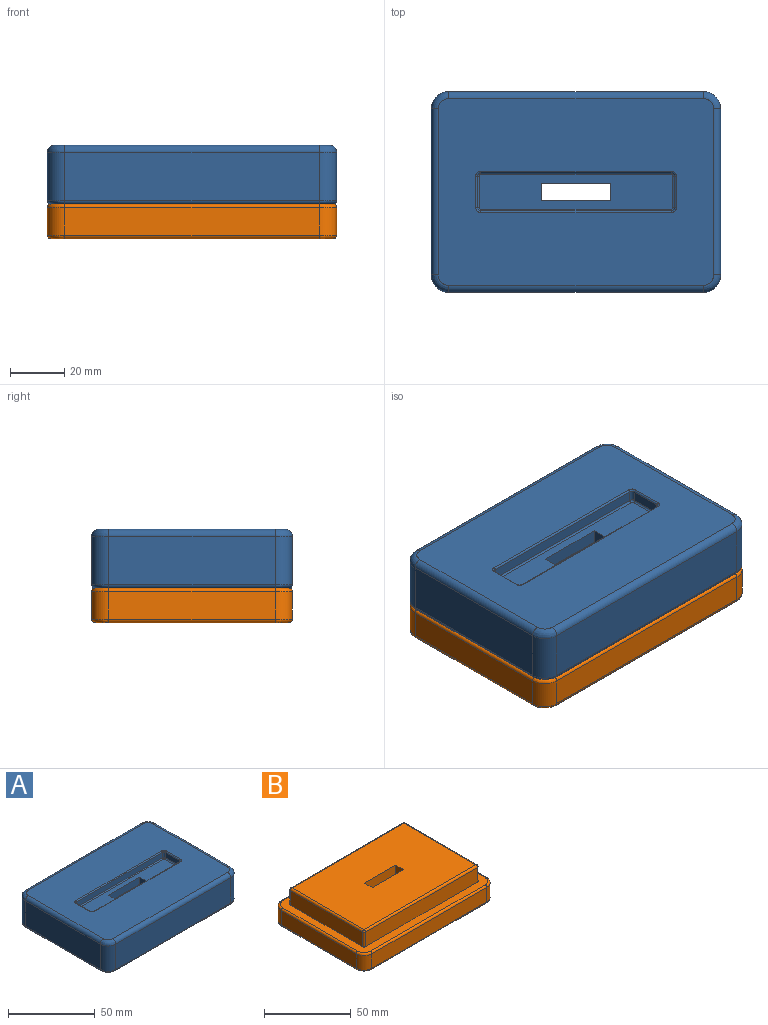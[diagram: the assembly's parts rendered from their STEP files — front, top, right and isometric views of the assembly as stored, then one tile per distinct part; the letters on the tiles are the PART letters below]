
ASSEMBLY  parts=2 mates=1
PART A: 72 faces, bbox 106.2x73.7x21.6 mm
  f0: plane 101.13x68.62mm, normal (0,0,1), area 5801.3mm2, adj f1,f2,f3,f4,f5,f6,f7,f8
  f1: cylinder r=2.54mm len=93.47mm, axis (1,0,0), area 372.9mm2, adj f0,f2,f8,f17
  f2: bspline ~6.35x6.35mm, area 34mm2, adj f0,f1,f3,f18
  f3: cylinder r=2.54mm len=60.96mm, axis (0,-1,0), area 243.2mm2, adj f0,f2,f4,f19
  f4: bspline ~6.35x6.35mm, area 34mm2, adj f0,f3,f5,f20
  f5: cylinder r=2.54mm len=93.47mm, axis (-1,0,0), area 372.9mm2, adj f0,f4,f6,f21
  f6: bspline ~6.35x6.35mm, area 34mm2, adj f0,f5,f7,f22
  f7: cylinder r=2.54mm len=60.96mm, axis (0,1,0), area 243.2mm2, adj f0,f6,f8,f23
  f8: bspline ~6.35x6.35mm, area 34mm2, adj f0,f1,f7,f24
  f9: bspline ~1.91x1.91mm, area 2.4mm2, adj f0,f10,f16,f25
  f10: cylinder r=0.64mm len=11.43mm, axis (0,1,0), area 11.4mm2, adj f0,f9,f11,f26
  f11: bspline ~1.91x1.91mm, area 2.4mm2, adj f0,f10,f12,f27
  f12: cylinder r=0.64mm len=69.85mm, axis (-1,0,0), area 69.7mm2, adj f0,f11,f13,f28
  f13: bspline ~1.91x1.91mm, area 2.4mm2, adj f0,f12,f14,f29
  f14: cylinder r=0.64mm len=11.43mm, axis (0,-1,0), area 11.4mm2, adj f0,f13,f15,f30
  f15: bspline ~1.91x1.91mm, area 2.4mm2, adj f0,f14,f16,f31
  f16: cylinder r=0.64mm len=69.85mm, axis (1,0,0), area 69.7mm2, adj f0,f9,f15,f32
  f17: plane 93.47x17.78mm, normal (0,1,0), area 1661.9mm2, adj f1,f18,f24,f33
  f18: cylinder r=6.35mm len=17.78mm, axis (0,0,-1), area 177.3mm2, adj f2,f17,f19,f34
  f19: plane 60.96x17.78mm, normal (1,0,0), area 1083.9mm2, adj f3,f18,f20,f35
  f20: cylinder r=6.35mm len=17.78mm, axis (0,0,-1), area 177.3mm2, adj f4,f19,f21,f36
  f21: plane 93.47x17.78mm, normal (0,-1,0), area 1661.9mm2, adj f5,f20,f22,f37
  f22: cylinder r=6.35mm len=17.78mm, axis (0,0,-1), area 177.3mm2, adj f6,f21,f23,f38
  f23: plane 60.96x17.78mm, normal (-1,0,0), area 1083.9mm2, adj f7,f22,f24,f39
  f24: cylinder r=6.35mm len=17.78mm, axis (0,0,-1), area 177.3mm2, adj f8,f17,f23,f40
  f25: cylinder r=1.27mm len=3.81mm, axis (0,0,1), area 7.6mm2, adj f9,f26,f32,f41
  f26: plane 11.43x3.81mm, normal (1,0,0), area 43.5mm2, adj f10,f25,f27,f42
  f27: cylinder r=1.27mm len=3.81mm, axis (0,0,1), area 7.6mm2, adj f11,f26,f28,f43
  f28: plane 69.85x3.81mm, normal (0,1,0), area 266.1mm2, adj f12,f27,f29,f44
  f29: cylinder r=1.27mm len=3.81mm, axis (0,0,1), area 7.6mm2, adj f13,f28,f30,f45
  f30: plane 11.43x3.81mm, normal (-1,0,0), area 43.5mm2, adj f14,f29,f31,f46
  f31: cylinder r=1.27mm len=3.81mm, axis (0,0,1), area 7.6mm2, adj f15,f30,f32,f47
  f32: plane 69.85x3.81mm, normal (0,-1,0), area 266.1mm2, adj f16,f25,f31,f48
  f33: cylinder r=1.27mm len=93.47mm, axis (-1,0,0), area 186.5mm2, adj f17,f34,f40,f49
  f34: bspline ~6.35x6.35mm, area 18.5mm2, adj f18,f33,f35,f49
  f35: cylinder r=1.27mm len=60.96mm, axis (0,1,0), area 121.6mm2, adj f19,f34,f36,f49
  f36: bspline ~6.35x6.35mm, area 18.5mm2, adj f20,f35,f37,f49
  f37: cylinder r=1.27mm len=93.47mm, axis (1,0,0), area 186.5mm2, adj f21,f36,f38,f49
  f38: bspline ~6.35x6.35mm, area 18.5mm2, adj f22,f37,f39,f49
  f39: cylinder r=1.27mm len=60.96mm, axis (0,-1,0), area 121.6mm2, adj f23,f38,f40,f49
  f40: bspline ~6.35x6.35mm, area 18.5mm2, adj f24,f33,f39,f49
  f41: bspline ~1.27x1.27mm, area 1.6mm2, adj f25,f42,f48,f50
  f42: cylinder r=0.64mm len=11.43mm, axis (0,1,0), area 11.4mm2, adj f26,f41,f43,f50
  f43: bspline ~1.27x1.27mm, area 1.6mm2, adj f27,f42,f44,f50
  f44: cylinder r=0.64mm len=69.85mm, axis (-1,0,0), area 69.7mm2, adj f28,f43,f45,f50
  f45: bspline ~1.27x1.27mm, area 1.6mm2, adj f29,f44,f46,f50
  f46: cylinder r=0.64mm len=11.43mm, axis (0,-1,0), area 11.4mm2, adj f30,f45,f47,f50
  f47: bspline ~1.27x1.27mm, area 1.6mm2, adj f31,f46,f48,f50
  f48: cylinder r=0.64mm len=69.85mm, axis (1,0,0), area 69.7mm2, adj f32,f41,f47,f50
  f49: plane 103.63x71.12mm, normal (0,0,-1), area 1651.5mm2, adj f33,f34,f35,f36,f37,f38,f39,f40
  f50: plane 71.13x12.71mm, normal (0,0,1), area 741.6mm2, adj f41,f42,f43,f44,f45,f46,f47,f48
  f51: plane 90.93x10.24mm, normal (0,-1,0), area 931.1mm2, adj f49,f52,f58,f63
  f52: cylinder r=1.27mm len=10.24mm, axis (0,0,1), area 20.4mm2, adj f49,f51,f53,f64
  f53: plane 58.42x10.24mm, normal (1,0,0), area 598.2mm2, adj f49,f52,f54,f65
  f54: cylinder r=1.27mm len=10.24mm, axis (0,0,1), area 20.4mm2, adj f49,f53,f55,f66
  f55: plane 90.93x10.24mm, normal (0,1,0), area 931.1mm2, adj f49,f54,f56,f67
  f56: cylinder r=1.27mm len=10.24mm, axis (0,0,1), area 20.4mm2, adj f49,f55,f57,f68
  f57: plane 58.42x10.24mm, normal (-1,0,0), area 598.2mm2, adj f49,f56,f58,f69
  f58: cylinder r=1.27mm len=10.24mm, axis (0,0,1), area 20.4mm2, adj f49,f51,f57,f70
  f59: plane 25.4x5mm, normal (0,-1,0), area 127mm2, adj f50,f60,f62,f71
  f60: plane 6.35x5mm, normal (-1,0,0), area 31.8mm2, adj f50,f59,f61,f71
  f61: plane 25.4x5mm, normal (0,1,0), area 127mm2, adj f50,f60,f62,f71
  f62: plane 6.35x5mm, normal (1,0,0), area 31.8mm2, adj f50,f59,f61,f71
  f63: cylinder r=1.27mm len=90.93mm, axis (-1,0,0), area 181.4mm2, adj f51,f64,f70,f71
  f64: bspline ~1.27x1.27mm, area 1.6mm2, adj f52,f63,f65
  f65: cylinder r=1.27mm len=58.42mm, axis (0,-1,0), area 116.5mm2, adj f53,f64,f66,f71
  f66: bspline ~1.27x1.27mm, area 2.6mm2, adj f54,f65,f67
  f67: cylinder r=1.27mm len=90.93mm, axis (1,0,0), area 181.4mm2, adj f55,f66,f68,f71
  f68: bspline ~1.27x1.27mm, area 1.6mm2, adj f56,f67,f69
  f69: cylinder r=1.27mm len=58.42mm, axis (0,1,0), area 116.5mm2, adj f57,f68,f70,f71
  f70: bspline ~1.27x1.27mm, area 1.6mm2, adj f58,f63,f69
  f71: plane 90.93x58.42mm, normal (0,0,-1), area 5151mm2, adj f59,f60,f61,f62,f63,f65,f67,f69
PART B: 71 faces, bbox 106.2x73.7x24.2 mm
  f0: plane 101.09x68.58mm, normal (0,0,-1), area 6759.1mm2, adj f1,f2,f3,f4,f5,f6,f7,f8
  f1: cylinder r=3.81mm len=10.16mm, axis (0,0,-1), area 60.8mm2, adj f0,f2,f8,f13
  f2: plane 60.96x10.16mm, normal (1,0,0), area 619.4mm2, adj f0,f1,f3,f13
  f3: cylinder r=3.81mm len=10.16mm, axis (0,0,-1), area 60.8mm2, adj f0,f2,f4,f13
  f4: plane 93.47x10.16mm, normal (0,-1,0), area 924.7mm2, adj f0,f3,f5,f13,f14,f15,f16,f17
  f5: cylinder r=3.81mm len=10.16mm, axis (0,0,-1), area 60.8mm2, adj f0,f4,f6,f13
  f6: plane 60.96x10.16mm, normal (-1,0,0), area 619.4mm2, adj f0,f5,f7,f13
  f7: cylinder r=3.81mm len=10.16mm, axis (0,0,-1), area 60.8mm2, adj f0,f6,f8,f13
  f8: plane 93.47x10.16mm, normal (0,1,0), area 949.7mm2, adj f0,f1,f7,f13
  f9: plane 25.4x14.05mm, normal (0,1,0), area 356.9mm2, adj f0,f10,f12,f21
  f10: plane 14.05x6.35mm, normal (-1,0,0), area 89.2mm2, adj f0,f9,f11,f21
  f11: plane 25.4x14.05mm, normal (0,-1,0), area 356.9mm2, adj f0,f10,f12,f21
  f12: plane 14.05x6.35mm, normal (1,0,0), area 89.2mm2, adj f0,f9,f11,f21
  f13: plane 103.63x71.12mm, normal (0,0,-1), area 418.2mm2, adj f1,f2,f3,f4,f5,f6,f7,f8
  f14: cylinder r=1.27mm len=1.27mm, axis (0,-1,0), area 2.5mm2, adj f4,f15,f20,f31
  f15: plane 2.46x1.27mm, normal (0,0,-1), area 3.1mm2, adj f4,f14,f16,f32
  f16: cylinder r=1.27mm len=1.27mm, axis (0,-1,0), area 2.5mm2, adj f4,f15,f17,f33
  f17: plane 2.46x1.27mm, normal (1,0,0), area 3.1mm2, adj f4,f16,f18,f34
  f18: cylinder r=1.27mm len=1.27mm, axis (0,-1,0), area 2.5mm2, adj f4,f13,f17,f35
  f19: cylinder r=1.27mm len=1.27mm, axis (0,1,0), area 2.5mm2, adj f4,f13,f20,f36
  f20: plane 2.46x1.27mm, normal (-1,0,0), area 3.1mm2, adj f4,f14,f19,f37
  f21: plane 90.93x58.42mm, normal (0,0,1), area 5151mm2, adj f9,f10,f11,f12,f38,f39,f40,f41
  f22: cylinder r=1.27mm len=42.97mm, axis (-1,0,0), area 85.7mm2, adj f13,f23,f36,f42
  f23: bspline ~6.35x6.35mm, area 18.5mm2, adj f13,f22,f24,f43
  f24: cylinder r=1.27mm len=60.96mm, axis (0,1,0), area 121.6mm2, adj f13,f23,f25,f44
  f25: bspline ~6.35x6.35mm, area 18.5mm2, adj f13,f24,f26,f45
  f26: cylinder r=1.27mm len=93.47mm, axis (1,0,0), area 186.5mm2, adj f13,f25,f27,f46
  f27: bspline ~6.35x6.35mm, area 18.5mm2, adj f13,f26,f28,f47
  f28: cylinder r=1.27mm len=60.96mm, axis (0,-1,0), area 121.6mm2, adj f13,f27,f29,f48
  f29: bspline ~6.35x6.35mm, area 18.5mm2, adj f13,f28,f30,f49
  f30: cylinder r=1.27mm len=42.97mm, axis (-1,0,0), area 85.7mm2, adj f13,f29,f35,f42
  f31: bspline ~2.54x2.54mm, area 5.4mm2, adj f14,f32,f37,f42
  f32: cylinder r=1.27mm len=2.46mm, axis (1,0,0), area 4.9mm2, adj f15,f31,f33,f42
  f33: bspline ~2.54x2.54mm, area 5.4mm2, adj f16,f32,f34,f42
  f34: cylinder r=1.27mm len=2.46mm, axis (0,0,1), area 4.9mm2, adj f17,f33,f35,f42
  f35: bspline ~1.27x1.27mm, area 2.5mm2, adj f18,f30,f34
  f36: bspline ~1.27x1.27mm, area 2.5mm2, adj f19,f22,f37
  f37: cylinder r=1.27mm len=2.46mm, axis (0,0,-1), area 4.9mm2, adj f20,f31,f36,f42
  f38: cylinder r=1.27mm len=90.93mm, axis (-1,0,0), area 181.4mm2, adj f21,f50,f51,f52
  f39: cylinder r=1.27mm len=58.42mm, axis (0,1,0), area 116.5mm2, adj f21,f52,f53,f54
  f40: cylinder r=1.27mm len=90.93mm, axis (1,0,0), area 181.4mm2, adj f21,f54,f55,f56
  f41: cylinder r=1.27mm len=58.42mm, axis (0,-1,0), area 116.5mm2, adj f21,f50,f56,f57
  f42: plane 93.47x10.16mm, normal (0,1,0), area 914.7mm2, adj f22,f30,f31,f32,f33,f34,f37,f43
  f43: cylinder r=6.35mm len=10.16mm, axis (0,0,-1), area 101.3mm2, adj f23,f42,f44,f59
  f44: plane 60.96x10.16mm, normal (1,0,0), area 619.4mm2, adj f24,f43,f45,f60
  f45: cylinder r=6.35mm len=10.16mm, axis (0,0,-1), area 101.3mm2, adj f25,f44,f46,f61
  f46: plane 93.47x10.16mm, normal (0,-1,0), area 949.7mm2, adj f26,f45,f47,f62
  f47: cylinder r=6.35mm len=10.16mm, axis (0,0,-1), area 101.3mm2, adj f27,f46,f48,f63
  f48: plane 60.96x10.16mm, normal (-1,0,0), area 619.4mm2, adj f28,f47,f49,f64
  f49: cylinder r=6.35mm len=10.16mm, axis (0,0,-1), area 101.3mm2, adj f29,f42,f48,f65
  f50: bspline ~1.27x1.27mm, area 2.5mm2, adj f38,f41,f66
  f51: plane 90.93x10.24mm, normal (0,-1,0), area 931.1mm2, adj f38,f66,f67,f68
  f52: bspline ~1.27x1.27mm, area 2.5mm2, adj f38,f39,f68
  f53: plane 58.42x10.24mm, normal (-1,0,0), area 598.2mm2, adj f39,f67,f68,f69
  f54: bspline ~1.27x1.27mm, area 2.5mm2, adj f39,f40,f69
  f55: plane 90.93x10.24mm, normal (0,1,0), area 931.1mm2, adj f40,f67,f69,f70
  f56: bspline ~1.27x1.27mm, area 2.5mm2, adj f40,f41,f70
  f57: plane 58.42x10.24mm, normal (1,0,0), area 598.2mm2, adj f41,f66,f67,f70
  f58: cylinder r=1.27mm len=93.47mm, axis (1,0,0), area 186.5mm2, adj f42,f59,f65,f67
  f59: bspline ~6.35x6.35mm, area 18.5mm2, adj f43,f58,f60,f67
  f60: cylinder r=1.27mm len=60.96mm, axis (0,-1,0), area 121.6mm2, adj f44,f59,f61,f67
  f61: bspline ~6.35x6.35mm, area 18.5mm2, adj f45,f60,f62,f67
  f62: cylinder r=1.27mm len=93.47mm, axis (-1,0,0), area 186.5mm2, adj f46,f61,f63,f67
  f63: bspline ~6.35x6.35mm, area 18.5mm2, adj f47,f62,f64,f67
  f64: cylinder r=1.27mm len=60.96mm, axis (0,1,0), area 121.6mm2, adj f48,f63,f65,f67
  f65: bspline ~6.35x6.35mm, area 18.5mm2, adj f49,f58,f64,f67
  f66: cylinder r=1.27mm len=10.24mm, axis (0,0,-1), area 20.4mm2, adj f50,f51,f57,f67
  f67: plane 103.63x71.12mm, normal (0,0,1), area 1651.5mm2, adj f51,f53,f55,f57,f58,f59,f60,f61
  f68: cylinder r=1.27mm len=10.24mm, axis (0,0,-1), area 20.4mm2, adj f51,f52,f53,f67
  f69: cylinder r=1.27mm len=10.24mm, axis (0,0,-1), area 20.4mm2, adj f53,f54,f55,f67
  f70: cylinder r=1.27mm len=10.24mm, axis (0,0,-1), area 20.4mm2, adj f55,f56,f57,f67
PLACE A t=(-0.53,0.22,1.39)mm
PLACE B t=(-0.53,0.22,-11.31)mm
MATE fastened A.f49 <-> B.f67  axis (0,0,-1) through (-0.53,0.22,1.39)mm
